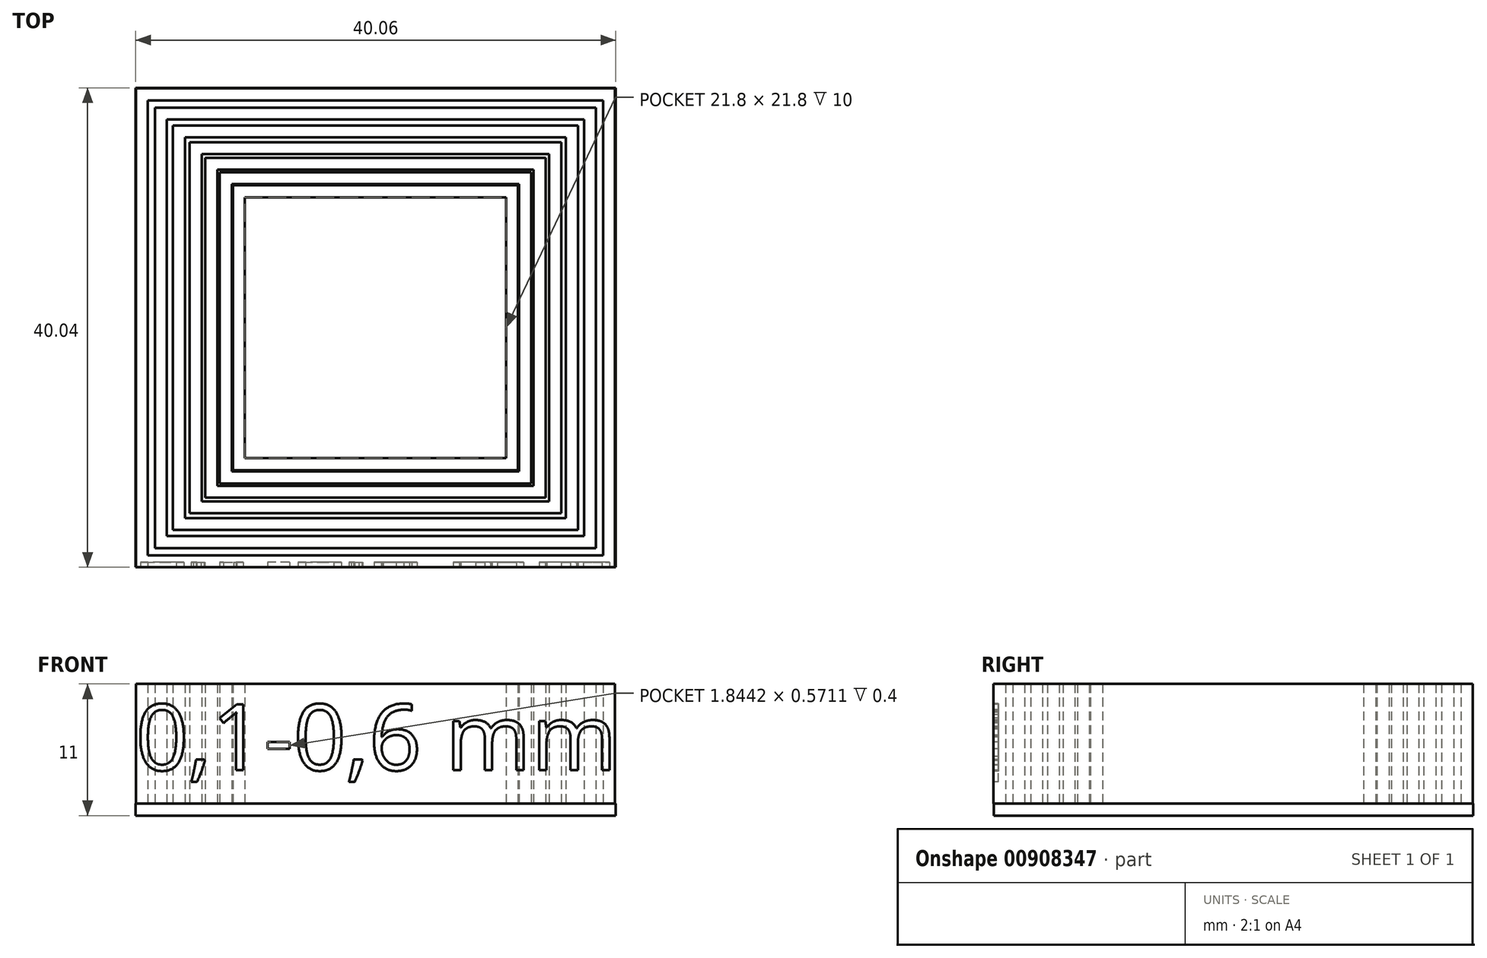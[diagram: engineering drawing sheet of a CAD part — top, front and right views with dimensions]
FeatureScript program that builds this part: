
annotation { "Feature Type Name" : "Feature", "Feature Type Description" : "" }
export const myFeature = defineFeature(function(context is Context, id is Id, definition is map)
    precondition{}
    {
        {
            var Q0;
            Q0=qCreatedBy(makeId("Top.planeOp"),FACE);
            var sketch = newSketch(context, id + "F0", { "sketchPlane" : qUnion([Q0])});
            skLineSegment(sketch, "E0.bottom", {"start": v(4.75, 2.34) * mm, "end": v(44.75, 2.34) * mm});
            skLineSegment(sketch, "E0.top", {"start": v(4.75, -37.66) * mm, "end": v(44.75, -37.66) * mm});
            skLineSegment(sketch, "E0.left", {"start": v(4.75, 2.34) * mm, "end": v(4.75, -37.66) * mm});
            skLineSegment(sketch, "E0.right", {"start": v(44.75, 2.34) * mm, "end": v(44.75, -37.66) * mm});
            skLineSegment(sketch, "E1.0", {"start": v(5.75, 1.34) * mm, "end": v(43.75, 1.34) * mm});
            skLineSegment(sketch, "E1.1", {"start": v(5.75, 1.34) * mm, "end": v(5.75, -36.66) * mm});
            skLineSegment(sketch, "E1.2", {"start": v(5.75, -36.66) * mm, "end": v(43.75, -36.66) * mm});
            skLineSegment(sketch, "E1.3", {"start": v(43.75, 1.34) * mm, "end": v(43.75, -36.66) * mm});
            skLineSegment(sketch, "E2.0", {"start": v(6.35, 0.74) * mm, "end": v(43.15, 0.74) * mm});
            skLineSegment(sketch, "E2.1", {"start": v(6.35, 0.74) * mm, "end": v(6.35, -36.06) * mm});
            skLineSegment(sketch, "E2.2", {"start": v(6.35, -36.06) * mm, "end": v(43.15, -36.06) * mm});
            skLineSegment(sketch, "E2.3", {"start": v(43.15, 0.74) * mm, "end": v(43.15, -36.06) * mm});
            skLineSegment(sketch, "E3.0", {"start": v(7.35, -0.26) * mm, "end": v(42.15, -0.26) * mm});
            skLineSegment(sketch, "E3.1", {"start": v(7.35, -0.26) * mm, "end": v(7.35, -35.06) * mm});
            skLineSegment(sketch, "E3.2", {"start": v(7.35, -35.06) * mm, "end": v(42.15, -35.06) * mm});
            skLineSegment(sketch, "E3.3", {"start": v(42.15, -0.26) * mm, "end": v(42.15, -35.06) * mm});
            skLineSegment(sketch, "E4.0", {"start": v(7.85, -0.76) * mm, "end": v(41.65, -0.76) * mm});
            skLineSegment(sketch, "E4.1", {"start": v(7.85, -0.76) * mm, "end": v(7.85, -34.56) * mm});
            skLineSegment(sketch, "E4.2", {"start": v(7.85, -34.56) * mm, "end": v(41.65, -34.56) * mm});
            skLineSegment(sketch, "E4.3", {"start": v(41.65, -0.76) * mm, "end": v(41.65, -34.56) * mm});
            skLineSegment(sketch, "E5.0", {"start": v(8.85, -1.76) * mm, "end": v(40.65, -1.76) * mm});
            skLineSegment(sketch, "E5.1", {"start": v(8.85, -1.76) * mm, "end": v(8.85, -33.56) * mm});
            skLineSegment(sketch, "E5.2", {"start": v(8.85, -33.56) * mm, "end": v(40.65, -33.56) * mm});
            skLineSegment(sketch, "E5.3", {"start": v(40.65, -1.76) * mm, "end": v(40.65, -33.56) * mm});
            skLineSegment(sketch, "E6.0", {"start": v(9.25, -2.16) * mm, "end": v(40.25, -2.16) * mm});
            skLineSegment(sketch, "E6.1", {"start": v(9.25, -2.16) * mm, "end": v(9.25, -33.16) * mm});
            skLineSegment(sketch, "E6.2", {"start": v(9.25, -33.16) * mm, "end": v(40.25, -33.16) * mm});
            skLineSegment(sketch, "E6.3", {"start": v(40.25, -2.16) * mm, "end": v(40.25, -33.16) * mm});
            skLineSegment(sketch, "E7.0", {"start": v(10.25, -3.16) * mm, "end": v(39.25, -3.16) * mm});
            skLineSegment(sketch, "E7.1", {"start": v(10.25, -3.16) * mm, "end": v(10.25, -32.16) * mm});
            skLineSegment(sketch, "E7.2", {"start": v(10.25, -32.16) * mm, "end": v(39.25, -32.16) * mm});
            skLineSegment(sketch, "E7.3", {"start": v(39.25, -3.16) * mm, "end": v(39.25, -32.16) * mm});
            skLineSegment(sketch, "E8.0", {"start": v(10.55, -3.46) * mm, "end": v(38.95, -3.46) * mm});
            skLineSegment(sketch, "E8.1", {"start": v(10.55, -3.46) * mm, "end": v(10.55, -31.86) * mm});
            skLineSegment(sketch, "E8.2", {"start": v(10.55, -31.86) * mm, "end": v(38.95, -31.86) * mm});
            skLineSegment(sketch, "E8.3", {"start": v(38.95, -3.46) * mm, "end": v(38.95, -31.86) * mm});
            skLineSegment(sketch, "E9.0", {"start": v(11.55, -4.46) * mm, "end": v(37.95, -4.46) * mm});
            skLineSegment(sketch, "E9.1", {"start": v(11.55, -4.46) * mm, "end": v(11.55, -30.86) * mm});
            skLineSegment(sketch, "E9.2", {"start": v(11.55, -30.86) * mm, "end": v(37.95, -30.86) * mm});
            skLineSegment(sketch, "E9.3", {"start": v(37.95, -4.46) * mm, "end": v(37.95, -30.86) * mm});
            skLineSegment(sketch, "E10.0", {"start": v(11.75, -4.66) * mm, "end": v(37.75, -4.66) * mm});
            skLineSegment(sketch, "E10.1", {"start": v(11.75, -4.66) * mm, "end": v(11.75, -30.66) * mm});
            skLineSegment(sketch, "E10.2", {"start": v(11.75, -30.66) * mm, "end": v(37.75, -30.66) * mm});
            skLineSegment(sketch, "E10.3", {"start": v(37.75, -4.66) * mm, "end": v(37.75, -30.66) * mm});
            skLineSegment(sketch, "E11.0", {"start": v(12.75, -5.66) * mm, "end": v(36.75, -5.66) * mm});
            skLineSegment(sketch, "E11.1", {"start": v(12.75, -5.66) * mm, "end": v(12.75, -29.66) * mm});
            skLineSegment(sketch, "E11.2", {"start": v(12.75, -29.66) * mm, "end": v(36.75, -29.66) * mm});
            skLineSegment(sketch, "E11.3", {"start": v(36.75, -5.66) * mm, "end": v(36.75, -29.66) * mm});
            skLineSegment(sketch, "E12.0", {"start": v(12.85, -5.76) * mm, "end": v(36.65, -5.76) * mm});
            skLineSegment(sketch, "E12.1", {"start": v(12.85, -5.76) * mm, "end": v(12.85, -29.56) * mm});
            skLineSegment(sketch, "E12.2", {"start": v(12.85, -29.56) * mm, "end": v(36.65, -29.56) * mm});
            skLineSegment(sketch, "E12.3", {"start": v(36.65, -5.76) * mm, "end": v(36.65, -29.56) * mm});
            skLineSegment(sketch, "E13.0", {"start": v(35.65, -6.76) * mm, "end": v(35.65, -28.56) * mm});
            skLineSegment(sketch, "E13.1", {"start": v(13.85, -6.76) * mm, "end": v(35.65, -6.76) * mm});
            skLineSegment(sketch, "E13.2", {"start": v(13.85, -6.76) * mm, "end": v(13.85, -28.56) * mm});
            skLineSegment(sketch, "E13.3", {"start": v(13.85, -28.56) * mm, "end": v(35.65, -28.56) * mm});
            skSolve(sketch);
        }
        {
            var Q0;
            Q0=qCreatedBy(makeId("Top.planeOp"),FACE);
            var sketch = newSketch(context, id + "F1", { "sketchPlane" : qUnion([Q0])});
            skLineSegment(sketch, "E14.bottom", {"start": v(4.74, 2.38) * mm, "end": v(44.8, 2.38) * mm});
            skLineSegment(sketch, "E14.top", {"start": v(4.74, -37.64) * mm, "end": v(44.8, -37.64) * mm});
            skLineSegment(sketch, "E14.left", {"start": v(4.74, 2.38) * mm, "end": v(4.74, -37.64) * mm});
            skLineSegment(sketch, "E14.right", {"start": v(44.8, 2.38) * mm, "end": v(44.8, -37.64) * mm});
            skSolve(sketch);
        }
        {
            var Q0;
            Q0 = qSketchRegion(id + "F1", true);
            extrude(context, id + "F2", {"entities" : qUnion([Q0]), "oppositeDirection" : true, "depth" : 1 * mm, "offsetDistance" : 25 * mm});
        }
        {
            var Q0;
            Q0=makeQuery(id+"F0.imprint","IMPRINT",FACE,{"disambiguationData":[TD([[makeQuery(id+"F0.imprint","IMPRINT",EDGE,{"derivedFrom":sQuery(id+"F0.wireOp",EDGE,"E0.bottom")}),-1.0]])]});
            var Q1;
            Q1=makeQuery(id+"F0.imprint","IMPRINT",FACE,{"disambiguationData":[TD([[makeQuery(id+"F0.imprint","IMPRINT",EDGE,{"derivedFrom":sQuery(id+"F0.wireOp",EDGE,"E2.0")}),-1.0]])]});
            var Q2;
            Q2=makeQuery(id+"F0.imprint","IMPRINT",FACE,{"disambiguationData":[TD([[makeQuery(id+"F0.imprint","IMPRINT",EDGE,{"derivedFrom":sQuery(id+"F0.wireOp",EDGE,"E4.0")}),-1.0]])]});
            var Q3;
            Q3=makeQuery(id+"F0.imprint","IMPRINT",FACE,{"disambiguationData":[TD([[makeQuery(id+"F0.imprint","IMPRINT",EDGE,{"derivedFrom":sQuery(id+"F0.wireOp",EDGE,"E6.0")}),-1.0]])]});
            var Q4;
            Q4=makeQuery(id+"F0.imprint","IMPRINT",FACE,{"disambiguationData":[TD([[makeQuery(id+"F0.imprint","IMPRINT",EDGE,{"derivedFrom":sQuery(id+"F0.wireOp",EDGE,"E8.0")}),-1.0]])]});
            var Q5;
            Q5=makeQuery(id+"F0.imprint","IMPRINT",FACE,{"disambiguationData":[TD([[makeQuery(id+"F0.imprint","IMPRINT",EDGE,{"derivedFrom":sQuery(id+"F0.wireOp",EDGE,"E10.0")}),-1.0]])]});
            var Q6;
            Q6=makeQuery(id+"F0.imprint","IMPRINT",FACE,{"disambiguationData":[TD([[makeQuery(id+"F0.imprint","IMPRINT",EDGE,{"derivedFrom":sQuery(id+"F0.wireOp",EDGE,"E12.0")}),-1.0]])]});
            extrude(context, id + "F3", {"entities" : qUnion([Q0, Q1, Q2, Q3, Q4, Q5, Q6]), "operationType" : NewBodyOperationType.ADD, "depth" : 10 * mm, "offsetDistance" : 25 * mm});
        }
        {
            var Q0;
            Q0=makeQuery(id+"F3.opExtrude","SWEPT_FACE",FACE,{"disambiguationData":[OSD([sQuery(id+"F0.wireOp",EDGE,"E0.top")])]});
            var sketch = newSketch(context, id + "F4", { "sketchPlane" : qUnion([Q0])});
            skText(sketch, "E15", { "text": "0,1-0,6 mm", "fontName": "OpenSans-Regular.ttf"});
            const initialGuessF4  = {"E15": [0.00475, 0.00279, 1, 0, 0.00554]};
            skSetInitialGuess(sketch, initialGuessF4);
            skSolve(sketch);
        }
        {
            var Q0;
            Q0 = qSketchRegion(id + "F4", true);
            extrude(context, id + "F5", {"entities" : qUnion([Q0]), "operationType" : NewBodyOperationType.REMOVE, "oppositeDirection" : true, "depth" : 0.4 * mm, "offsetDistance" : 25 * mm});
        }
    });
